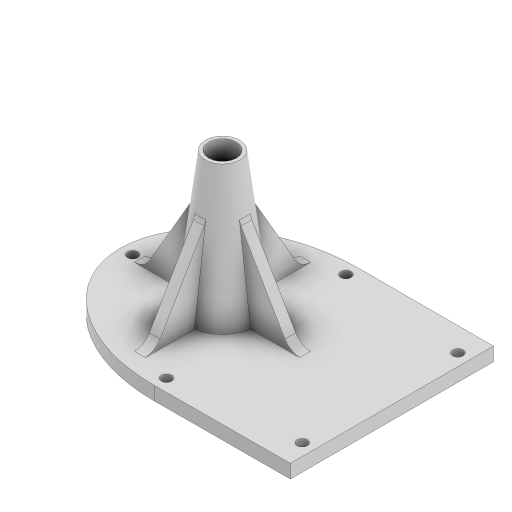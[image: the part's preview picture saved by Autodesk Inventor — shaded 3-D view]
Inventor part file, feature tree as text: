
AUTODESK INVENTOR PART (.ipt)
format: ipt  version: 2024 (Build 280153000, 153)  size: 907,264 bytes
history: native  units: in
note: dims shown in document units (in); Inventor stores cm internally (conversion verified against a paired STEP export)
features: sketch x8, extrude x5, projected_geometry x3, fillet x2, plane x1, revolve x1
ambient origin geometry x8: Origin, YZ Plane, XZ Plane, XY Plane, X Axis, Y Axis, Z Axis, Center Point
bodies: Solid1 (feature_tree)
feature tree (20):
  extrude  "Extrusion1"  Depth=0.42in
  extrude  "Extrusion3"  Depth=0.5in
  sketch  "Sketch6"  dims[d23=0.35in d24=0.35in]
  extrude  "Extrusion4"  Depth=0.41in
  extrude  "Extrusion5"  Depth=0.175in
  extrude  "Extrusion6"  Depth=0.35in
  sketch  "Sketch9"  dims[d32=0.35in]
  plane  "Work Plane2"
  sketch  "Sketch11"  dims[d33=0.3504in d34=1.8247in d35=3.825in d37=1.5065in d38=0.13in d39=0.15in d40=0.15in d41=0.15in d42=0.15in d43=1.9in d44=0.0in d46=1.0in d47=1.0in d48=1.0in d49=0.0in d50=1.0in d51=0.08in d52=1.5748in d54=360.0deg d56=1.25in d57=0.0in d58=0.01in d59=0.125in d60=-0.08in d61=90.0deg d62=0.25in d63=0.25in d70=1.503in d72=0.155in d73=0.155in d74=0.155in d75=0.155in d76=0.155in]
  revolve  "Revolution1"  [1 undecoded]
  fillet  "Fillet1"  Radius=0.175in
  fillet  "Fillet2"  Radius=3.825in
  sketch  "Sketch1"  dims[d0=0.2in d1=0.0in d13=0.42in]
  sketch  "Sketch3"  dims[d14=1.0in d15=0.5in]
  sketch  "Sketch4"  dims[d17=2.0in d18=-0.0481in d19=0.41in]
  sketch  "Sketch5"  dims[d20=1.9in d21=0.0in d22=0.175in]
  projected_geometry  "Projected Loop16"
  sketch  "Sketch8"  dims[d25=0.175in d26=0.175in d27=0.175in d29=3.825in]
  projected_geometry  "Projected Loop17"
  projected_geometry  "Projected Loop18"
note: 1 required parameter value undecoded (feature->parameter linkage not recoverable at this tier; creation-order binding heuristic only, values carry confidence <= 0.55)
